FCSTD DOCUMENT  (FreeCAD 0.17R13541 (Git))
Label: Xtrusion5mmx5.5
License: All rights reserved
LicenseURL: http://en.wikipedia.org/wiki/All_rights_reserved
objects: Sketcher::SketchObject×1
note: 1 computed .brp shape members not serialized (recipe doc carries the construction recipe); baked Part::Feature solids carry a one-line shape summary decoded from their .brp

FEATURE [Sketcher::SketchObject] Sketch
  sketch-geometry (32):
    g0: LineSegment StartX=-75.2529 StartY=-27.1569 StartZ=0 EndX=-61.4244 EndY=-27.1569 EndZ=0
    g1: LineSegment StartX=-61.4244 StartY=-27.1569 StartZ=0 EndX=-66.9244 EndY=-21.6569 EndZ=0
    g2: LineSegment StartX=-66.9244 StartY=-21.6569 StartZ=0 EndX=-50.9244 EndY=-21.6569 EndZ=0
    g3: LineSegment StartX=-50.9244 StartY=-21.6569 StartZ=0 EndX=-56.4244 EndY=-27.1569 EndZ=0
    g4: LineSegment StartX=-56.4244 StartY=-27.1569 StartZ=0 EndX=-42.596 EndY=-27.1569 EndZ=0
    g5: LineSegment StartX=-42.596 StartY=-27.1569 StartZ=0 EndX=-42.596 EndY=-13.3284 EndZ=0
    g6: LineSegment StartX=-42.596 StartY=-13.3284 StartZ=0 EndX=-48.096 EndY=-18.8284 EndZ=0
    g7: LineSegment StartX=-48.096 StartY=-18.8284 StartZ=0 EndX=-48.096 EndY=-2.82843 EndZ=0
    g8: LineSegment StartX=-48.096 StartY=-2.82843 StartZ=0 EndX=-42.596 EndY=-8.32843 EndZ=0
    g9: LineSegment StartX=-42.596 StartY=-8.32843 StartZ=0 EndX=-42.596 EndY=5.5 EndZ=0
    g10: LineSegment StartX=-42.596 StartY=5.5 StartZ=0 EndX=-56.4244 EndY=5.5 EndZ=0
    g11: LineSegment StartX=-56.4244 StartY=5.5 StartZ=0 EndX=-50.9244 EndY=0 EndZ=0
    g12: LineSegment StartX=-50.9244 StartY=0 StartZ=0 EndX=-66.9244 EndY=0 EndZ=0
    g13: LineSegment StartX=-66.9244 StartY=0 StartZ=0 EndX=-61.4244 EndY=5.5 EndZ=0
    g14: LineSegment StartX=-61.4244 StartY=5.5 StartZ=0 EndX=-75.2529 EndY=5.5 EndZ=0
    g15: LineSegment StartX=-75.2529 StartY=5.5 StartZ=0 EndX=-75.2529 EndY=-8.32843 EndZ=0
    g16: LineSegment StartX=-75.2529 StartY=-8.32843 StartZ=0 EndX=-69.7529 EndY=-2.82843 EndZ=0
    g17: LineSegment StartX=-69.7529 StartY=-2.82843 StartZ=0 EndX=-69.7529 EndY=-18.8284 EndZ=0
    g18: LineSegment StartX=-69.7529 StartY=-18.8284 StartZ=0 EndX=-75.2529 EndY=-13.3284 EndZ=0
    g19: LineSegment StartX=-75.2529 StartY=-13.3284 StartZ=0 EndX=-75.2529 EndY=-27.1569 EndZ=0
    g20: LineSegment [constr] StartX=-61.4244 StartY=-27.1569 StartZ=0 EndX=-56.4244 EndY=-27.1569 EndZ=0
    g21: LineSegment [constr] StartX=-61.4244 StartY=5.5 StartZ=0 EndX=-56.4244 EndY=5.5 EndZ=0
    g22: LineSegment [constr] StartX=-42.596 StartY=-8.32843 StartZ=0 EndX=-42.596 EndY=-13.3284 EndZ=0
    g23: LineSegment [constr] StartX=-75.2529 StartY=-8.32843 StartZ=0 EndX=-75.2529 EndY=-13.3284 EndZ=0
    g24: LineSegment [constr] StartX=-66.9244 StartY=-21.6569 StartZ=0 EndX=-66.9244 EndY=-27.1569 EndZ=0
    g25: LineSegment [constr] StartX=-69.7529 StartY=-18.8284 StartZ=0 EndX=-75.2529 EndY=-18.8284 EndZ=0
    g26: LineSegment [constr] StartX=-66.9244 StartY=5.5 StartZ=0 EndX=-66.9244 EndY=0 EndZ=0
    g27: LineSegment [constr] StartX=-48.096 StartY=-2.82843 StartZ=0 EndX=-42.596 EndY=-2.82843 EndZ=0
    g28: LineSegment [constr] StartX=-69.7529 StartY=-2.82843 StartZ=0 EndX=-66.9244 EndY=0 EndZ=0
    g29: LineSegment [constr] StartX=-69.7529 StartY=-18.8284 StartZ=0 EndX=-66.1469 EndY=-20.5596 EndZ=0
    g30: LineSegment [constr] StartX=-50.9244 StartY=-21.6569 StartZ=0 EndX=-48.096 EndY=-18.8284 EndZ=0
    g31: LineSegment [constr] StartX=-50.9244 StartY=0 StartZ=0 EndX=-48.096 EndY=-2.82843 EndZ=0
  constraints (93):
    c: Horizontal(g0)
    c: Coincident(g0,g1)
    c: Coincident(g1,g2)
    c: Horizontal(g2)
    c: Coincident(g2,g3)
    c: Coincident(g3,g4)
    c: Horizontal(g4)
    c: Coincident(g4,g5)
    c: Vertical(g5)
    c: Coincident(g5,g6)
    c: Coincident(g6,g7)
    c: Vertical(g7)
    c: Coincident(g7,g8)
    c: Coincident(g8,g9)
    c: Vertical(g9)
    c: Coincident(g9,g10)
    c: Horizontal(g10)
    c: Coincident(g10,g11)
    c: Coincident(g11,g12)
    c: PointOnObject(g12,g-1)
    c: Horizontal(g12)
    c: Coincident(g12,g13)
    c: Coincident(g13,g14)
    c: Horizontal(g14)
    c: Coincident(g14,g15)
    c: Vertical(g15)
    c: Coincident(g15,g16)
    c: Coincident(g16,g17)
    c: Vertical(g17)
    c: Coincident(g17,g18)
    c: Coincident(g18,g19)
    c: Vertical(g19)
    c: Equal(g14,g10)
    c: Equal(g10,g9)
    c: Equal(g9,g5)
    c: Equal(g5,g4)
    c: Equal(g4,g0)
    c: Equal(g0,g19)
    c: Equal(g19,g15)
    c: Equal(g17,g12)
    c: Equal(g12,g7)
    c: Equal(g7,g2)
    c: Angle(g1,g0) = 0.785398
    c: Angle(g19,g18) = 0.785398
    c: Angle(g4,g3) = 0.785398
    c: Angle(g6,g5) = 0.785398
    c: Angle(g9,g8) = 0.785398
    c: Angle(g11,g10) = 0.785398
    c: Angle(g14,g13) = 0.785398
    c: Angle(g16,g15) = 0.785398
    c: Equal(g16,g13)
    c: Equal(g13,g11)
    c: Equal(g11,g8)
    c: Equal(g8,g6)
    c: Equal(g6,g3)
    c: Equal(g3,g1)
    c: Equal(g1,g18)
    c: Coincident(g20,g0)
    c: Coincident(g20,g3)
    c: Coincident(g21,g13)
    c: Coincident(g21,g10)
    c: Coincident(g22,g8)
    c: Coincident(g22,g5)
    c: Coincident(g23,g15)
    c: Coincident(g23,g18)
    c: Equal(g23,g21)
    c: Equal(g21,g22)
    c: Equal(g22,g20)
    c: Distance(g21) = 5
    c: Coincident(g24,g1)
    c: PointOnObject(g24,g0)
    c: Vertical(g24)
    c: Coincident(g25,g17)
    c: PointOnObject(g25,g19)
    c: Horizontal(g25)
    c: PointOnObject(g26,g14)
    c: Coincident(g26,g12)
    c: Coincident(g27,g7)
    c: Horizontal(g27)
    c: Equal(g27,g26)
    c: Equal(g26,g25)
    c: Distance(g26) = 5.5
    c: Coincident(g28,g16)
    c: Coincident(g28,g12)
    c: Coincident(g29,g17)
    c: Coincident(g30,g2)
    c: Coincident(g30,g6)
    c: Coincident(g31,g11)
    c: Coincident(g31,g7)
    c: Equal(g30,g29)
    c: Equal(g29,g28)
    c: Equal(g28,g31)
    c: Distance(g31) = 4
